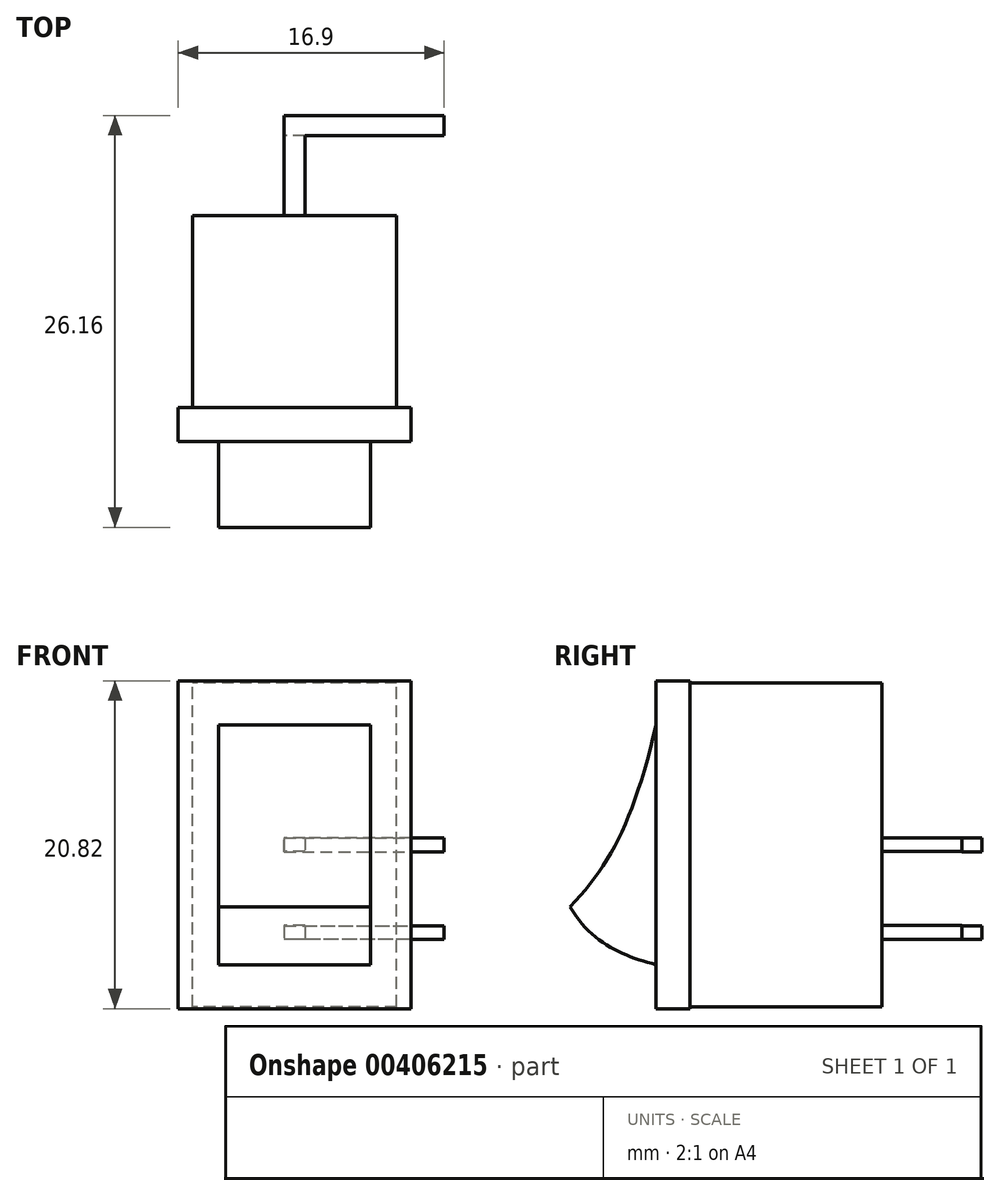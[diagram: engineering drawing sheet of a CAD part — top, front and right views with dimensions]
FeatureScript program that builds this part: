
annotation { "Feature Type Name" : "Feature", "Feature Type Description" : "" }
export const myFeature = defineFeature(function(context is Context, id is Id, definition is map)
    precondition{}
    {
        {
            var Q0;
            Q0=qCreatedBy(makeId("Front.planeOp"),FACE);
            var sketch = newSketch(context, id + "F0", { "sketchPlane" : qUnion([Q0])});
            skLineSegment(sketch, "E0.bottom", {"start": v(4.83, -7.62) * mm, "end": v(-4.83, -7.62) * mm});
            skLineSegment(sketch, "E0.top", {"start": v(4.83, 7.62) * mm, "end": v(-4.83, 7.62) * mm});
            skLineSegment(sketch, "E0.left", {"start": v(4.83, -7.62) * mm, "end": v(4.83, 7.62) * mm});
            skLineSegment(sketch, "E0.right", {"start": v(-4.83, -7.62) * mm, "end": v(-4.83, 7.62) * mm});
            skPoint(sketch, "E0.middle", {"position": v(0, 0) * mm});
            skLineSegment(sketch, "E1.bottom", {"start": v(6.48, -10.29) * mm, "end": v(-6.48, -10.29) * mm});
            skLineSegment(sketch, "E1.top", {"start": v(6.48, 10.29) * mm, "end": v(-6.48, 10.29) * mm});
            skLineSegment(sketch, "E1.left", {"start": v(6.48, -10.29) * mm, "end": v(6.48, 10.29) * mm});
            skLineSegment(sketch, "E1.right", {"start": v(-6.48, -10.29) * mm, "end": v(-6.48, 10.29) * mm});
            skLineSegment(sketch, "E2.bottom", {"start": v(7.4, -10.41) * mm, "end": v(-7.4, -10.41) * mm});
            skLineSegment(sketch, "E2.top", {"start": v(7.4, 10.41) * mm, "end": v(-7.4, 10.41) * mm});
            skLineSegment(sketch, "E2.left", {"start": v(7.4, -10.41) * mm, "end": v(7.4, 10.41) * mm});
            skLineSegment(sketch, "E2.right", {"start": v(-7.4, -10.41) * mm, "end": v(-7.4, 10.41) * mm});
            skSolve(sketch);
        }
        {
            var Q0;
            {var subQ9=sQuery(id+"F0.wireOp",EDGE,"E1.bottom");Q0=makeQuery(id+"F0.imprint","IMPRINT",FACE,{"disambiguationData":[TD([[makeQuery(id+"F0.imprint","IMPRINT",EDGE,{"derivedFrom":subQ9}),1.0]])]});}
            var Q1;
            {var subQ0=sQuery(id+"F0.wireOp",EDGE,"90RDVzbx-pbEp-RKpr-ZJp7-oBMPYdw4tj7I");var subQ1=sQuery(id+"F0.wireOp",EDGE,"E1.left");var subQ2=makeQuery(id+"F0.imprint","INTERSECT",VERTEX,{"derivedFrom":[subQ1,subQ0]});Q1=makeQuery(id+"F0.imprint","IMPRINT",FACE,{"disambiguationData":[TD([[makeQuery(id+"F0.imprint","IMPRINT",EDGE,{"disambiguationData":[TD([[subQ2,-1.0]])],"derivedFrom":subQ1}),-1.0]])]});}
            var Q2;
            {var subQ0=sQuery(id+"F0.wireOp",EDGE,"RYyEcB3p-NkHa-Vshw-HssV-5ZcSdsTJxcc6");var subQ1=sQuery(id+"F0.wireOp",EDGE,"E1.left");var subQ2=makeQuery(id+"F0.imprint","INTERSECT",VERTEX,{"derivedFrom":[subQ1,subQ0]});Q2=makeQuery(id+"F0.imprint","IMPRINT",FACE,{"disambiguationData":[TD([[makeQuery(id+"F0.imprint","IMPRINT",EDGE,{"disambiguationData":[TD([[subQ2,-1.0]])],"derivedFrom":subQ1}),-1.0]])]});}
            var Q3;
            {var subQ0=sQuery(id+"F0.wireOp",EDGE,"IALBhpj6-41kV-CNMg-Mphc-D1CcIKWyzzbN");var subQ1=sQuery(id+"F0.wireOp",EDGE,"E1.left");var subQ2=makeQuery(id+"F0.imprint","INTERSECT",VERTEX,{"derivedFrom":[subQ1,subQ0]});Q3=makeQuery(id+"F0.imprint","IMPRINT",FACE,{"disambiguationData":[TD([[makeQuery(id+"F0.imprint","IMPRINT",EDGE,{"disambiguationData":[TD([[subQ2,-1.0]])],"derivedFrom":subQ1}),-1.0]])]});}
            var Q4;
            {var subQ0=sQuery(id+"F0.wireOp",EDGE,"IALBhpj6-41kV-CNMg-Mphc-D1CcIKWyzzbN");var subQ1=sQuery(id+"F0.wireOp",EDGE,"E0.left");var subQ2=makeQuery(id+"F0.imprint","INTERSECT",VERTEX,{"derivedFrom":[subQ1,subQ0]});Q4=makeQuery(id+"F0.imprint","IMPRINT",FACE,{"disambiguationData":[TD([[makeQuery(id+"F0.imprint","IMPRINT",EDGE,{"disambiguationData":[TD([[subQ2,-1.0]])],"derivedFrom":subQ1}),-1.0]])]});}
            var Q5;
            {var subQ0=sQuery(id+"F0.wireOp",EDGE,"90RDVzbx-pbEp-RKpr-ZJp7-oBMPYdw4tj7I");var subQ1=sQuery(id+"F0.wireOp",EDGE,"E0.left");var subQ2=makeQuery(id+"F0.imprint","INTERSECT",VERTEX,{"derivedFrom":[subQ1,subQ0]});Q5=makeQuery(id+"F0.imprint","IMPRINT",FACE,{"disambiguationData":[TD([[makeQuery(id+"F0.imprint","IMPRINT",EDGE,{"disambiguationData":[TD([[subQ2,-1.0]])],"derivedFrom":subQ1}),-1.0]])]});}
            extrude(context, id + "F1", {"entities" : qUnion([Q0, Q1, Q2, Q3, Q4, Q5]), "depth" : 2.16 * mm});
        }
        {
            var Q0;
            {var subQ7=sQuery(id+"F0.wireOp",EDGE,"E0.bottom");Q0=makeQuery(id+"F0.imprint","IMPRINT",FACE,{"disambiguationData":[TD([[makeQuery(id+"F0.imprint","IMPRINT",EDGE,{"derivedFrom":subQ7}),1.0]])]});}
            var Q1;
            {var subQ0=sQuery(id+"F0.wireOp",EDGE,"RYyEcB3p-NkHa-Vshw-HssV-5ZcSdsTJxcc6");var subQ1=sQuery(id+"F0.wireOp",EDGE,"E0.left");var subQ2=makeQuery(id+"F0.imprint","INTERSECT",VERTEX,{"derivedFrom":[subQ1,subQ0]});Q1=makeQuery(id+"F0.imprint","IMPRINT",FACE,{"disambiguationData":[TD([[makeQuery(id+"F0.imprint","IMPRINT",EDGE,{"disambiguationData":[TD([[subQ2,-1.0]])],"derivedFrom":subQ1}),-1.0]])]});}
            extrude(context, id + "F2", {"entities" : qUnion([Q0, Q1]), "operationType" : NewBodyOperationType.ADD, "depth" : 2.16 * mm});
        }
        {
            var Q0;
            {var subQ7=sQuery(id+"F0.wireOp",EDGE,"E0.bottom");Q0=makeQuery(id+"F0.imprint","IMPRINT",FACE,{"disambiguationData":[TD([[makeQuery(id+"F0.imprint","IMPRINT",EDGE,{"derivedFrom":subQ7}),-1.0]])]});}
            var Q1;
            {var subQ5=sQuery(id+"F0.wireOp",EDGE,"Gz4o4iUm-N9Nq-rkyt-yYwc-V763e9riTsWX");Q1=makeQuery(id+"F0.imprint","IMPRINT",FACE,{"disambiguationData":[TD([[makeQuery(id+"F0.imprint","IMPRINT",EDGE,{"derivedFrom":subQ5}),-1.0]])]});}
            var Q2;
            {var subQ5=sQuery(id+"F0.wireOp",EDGE,"LmZJG6sO-EFJF-EY5x-AEzQ-LZyFRe2Vw74O");Q2=makeQuery(id+"F0.imprint","IMPRINT",FACE,{"disambiguationData":[TD([[makeQuery(id+"F0.imprint","IMPRINT",EDGE,{"derivedFrom":subQ5}),1.0]])]});}
            extrude(context, id + "F3", {"entities" : qUnion([Q0, Q1, Q2]), "operationType" : NewBodyOperationType.ADD, "depth" : 7.62 * mm});
        }
        {
            var Q0;
            {var subQ7=sQuery(id+"F0.wireOp",EDGE,"E0.bottom");Q0=makeQuery(id+"F0.imprint","IMPRINT",FACE,{"disambiguationData":[TD([[makeQuery(id+"F0.imprint","IMPRINT",EDGE,{"derivedFrom":subQ7}),1.0]])]});}
            var Q1;
            {var subQ0=sQuery(id+"F0.wireOp",EDGE,"90RDVzbx-pbEp-RKpr-ZJp7-oBMPYdw4tj7I");var subQ1=sQuery(id+"F0.wireOp",EDGE,"E0.left");var subQ2=makeQuery(id+"F0.imprint","INTERSECT",VERTEX,{"derivedFrom":[subQ1,subQ0]});Q1=makeQuery(id+"F0.imprint","IMPRINT",FACE,{"disambiguationData":[TD([[makeQuery(id+"F0.imprint","IMPRINT",EDGE,{"disambiguationData":[TD([[subQ2,-1.0]])],"derivedFrom":subQ1}),-1.0]])]});}
            var Q2;
            {var subQ0=sQuery(id+"F0.wireOp",EDGE,"RYyEcB3p-NkHa-Vshw-HssV-5ZcSdsTJxcc6");var subQ1=sQuery(id+"F0.wireOp",EDGE,"E0.left");var subQ2=makeQuery(id+"F0.imprint","INTERSECT",VERTEX,{"derivedFrom":[subQ1,subQ0]});Q2=makeQuery(id+"F0.imprint","IMPRINT",FACE,{"disambiguationData":[TD([[makeQuery(id+"F0.imprint","IMPRINT",EDGE,{"disambiguationData":[TD([[subQ2,-1.0]])],"derivedFrom":subQ1}),-1.0]])]});}
            var Q3;
            {var subQ0=sQuery(id+"F0.wireOp",EDGE,"IALBhpj6-41kV-CNMg-Mphc-D1CcIKWyzzbN");var subQ1=sQuery(id+"F0.wireOp",EDGE,"E0.left");var subQ2=makeQuery(id+"F0.imprint","INTERSECT",VERTEX,{"derivedFrom":[subQ1,subQ0]});Q3=makeQuery(id+"F0.imprint","IMPRINT",FACE,{"disambiguationData":[TD([[makeQuery(id+"F0.imprint","IMPRINT",EDGE,{"disambiguationData":[TD([[subQ2,-1.0]])],"derivedFrom":subQ1}),-1.0]])]});}
            var Q4;
            {var subQ7=sQuery(id+"F0.wireOp",EDGE,"E0.bottom");Q4=makeQuery(id+"F0.imprint","IMPRINT",FACE,{"disambiguationData":[TD([[makeQuery(id+"F0.imprint","IMPRINT",EDGE,{"derivedFrom":subQ7}),-1.0]])]});}
            var Q5;
            {var subQ5=sQuery(id+"F0.wireOp",EDGE,"Gz4o4iUm-N9Nq-rkyt-yYwc-V763e9riTsWX");Q5=makeQuery(id+"F0.imprint","IMPRINT",FACE,{"disambiguationData":[TD([[makeQuery(id+"F0.imprint","IMPRINT",EDGE,{"derivedFrom":subQ5}),-1.0]])]});}
            var Q6;
            {var subQ5=sQuery(id+"F0.wireOp",EDGE,"LmZJG6sO-EFJF-EY5x-AEzQ-LZyFRe2Vw74O");Q6=makeQuery(id+"F0.imprint","IMPRINT",FACE,{"disambiguationData":[TD([[makeQuery(id+"F0.imprint","IMPRINT",EDGE,{"derivedFrom":subQ5}),1.0]])]});}
            extrude(context, id + "F4", {"entities" : qUnion([Q0, Q1, Q2, Q3, Q4, Q5, Q6]), "operationType" : NewBodyOperationType.ADD, "oppositeDirection" : true, "depth" : 12.2 * mm});
        }
        {
            var Q0;
            Q0=makeQuery(id+"F3.opExtrude","SWEPT_FACE",FACE,{"disambiguationData":[OSD([sQuery(id+"F0.wireOp",EDGE,"E0.right")])]});
            var sketch = newSketch(context, id + "F5", { "sketchPlane" : qUnion([Q0])});
            skFitSpline(sketch, "E3", {"points": [v(2.16, -7.62) * mm, v(7.62, -3.94) * mm], "startDerivative": vector(6.36, 1.68) * mm, "endDerivative": vector(3.97, 6.9) * mm});
            skFitSpline(sketch, "E4", {"points": [v(7.62, -3.94) * mm, v(2.16, 7.62) * mm], "startDerivative": vector(-7.88, 8.25) * mm, "endDerivative": vector(-4.33, 18.23) * mm});
            skSolve(sketch);
        }
        {
            var Q0;
            {var subQ0=sQuery(id+"F5.wireOp",EDGE,"E3");Q0=makeQuery(id+"F5.imprint","IMPRINT",FACE,{"disambiguationData":[TD([[makeQuery(id+"F5.imprint","IMPRINT",EDGE,{"derivedFrom":subQ0}),-1.0]])]});}
            extrude(context, id + "F6", {"entities" : qUnion([Q0]), "operationType" : NewBodyOperationType.REMOVE, "oppositeDirection" : true, "depth" : 25.4 * mm});
        }
        {
            var Q0;
            {var subQ0=sQuery(id+"F5.wireOp",EDGE,"E4");Q0=makeQuery(id+"F5.imprint","IMPRINT",FACE,{"disambiguationData":[TD([[makeQuery(id+"F5.imprint","IMPRINT",EDGE,{"derivedFrom":subQ0}),-1.0]])]});}
            extrude(context, id + "F7", {"entities" : qUnion([Q0]), "operationType" : NewBodyOperationType.REMOVE, "oppositeDirection" : true, "depth" : 25.4 * mm});
        }
        {
            var Q0;
            Q0=makeQuery(id+"F4.opExtrude","CAP_FACE",FACE,{"disambiguationData":[OSD([sQuery(id+"F0.wireOp",EDGE,"E1.bottom"),sQuery(id+"F0.wireOp",EDGE,"E1.top"),sQuery(id+"F0.wireOp",EDGE,"E1.left"),sQuery(id+"F0.wireOp",EDGE,"E1.right")])],"isStart":false});
            var sketch = newSketch(context, id + "F8", { "sketchPlane" : qUnion([Q0])});
            skLineSegment(sketch, "E5", {"start": v(0, 0) * mm, "end": v(0, 0) * mm});
            skLineSegment(sketch, "E6.bottom", {"start": v(-0.66, 0.43) * mm, "end": v(0.66, 0.43) * mm});
            skLineSegment(sketch, "E6.top", {"start": v(-0.66, -0.43) * mm, "end": v(0.66, -0.43) * mm});
            skLineSegment(sketch, "E6.left", {"start": v(-0.66, 0.43) * mm, "end": v(-0.66, -0.43) * mm});
            skLineSegment(sketch, "E6.right", {"start": v(0.66, 0.43) * mm, "end": v(0.66, -0.43) * mm});
            skPoint(sketch, "E6.middle", {"position": v(0, 0) * mm});
            skLineSegment(sketch, "E7.bottom", {"start": v(-0.66, -5.13) * mm, "end": v(0.66, -5.13) * mm});
            skLineSegment(sketch, "E7.top", {"start": v(-0.66, -6) * mm, "end": v(0.66, -6) * mm});
            skLineSegment(sketch, "E7.left", {"start": v(-0.66, -5.13) * mm, "end": v(-0.66, -6) * mm});
            skLineSegment(sketch, "E7.right", {"start": v(0.66, -5.13) * mm, "end": v(0.66, -6) * mm});
            skPoint(sketch, "E7.middle", {"position": v(0, -5.57) * mm});
            skSolve(sketch);
        }
        {
            var Q0;
            Q0=makeQuery(id+"F8.imprint","IMPRINT",FACE,{"disambiguationData":[TD([[makeQuery(id+"F8.imprint","IMPRINT",EDGE,{"derivedFrom":sQuery(id+"F8.wireOp",EDGE,"E6.bottom")}),-1.0]])]});
            var Q1;
            Q1=makeQuery(id+"F8.imprint","IMPRINT",FACE,{"disambiguationData":[TD([[makeQuery(id+"F8.imprint","IMPRINT",EDGE,{"derivedFrom":sQuery(id+"F8.wireOp",EDGE,"E7.bottom")}),-1.0]])]});
            extrude(context, id + "F9", {"entities" : qUnion([Q0, Q1]), "operationType" : NewBodyOperationType.ADD, "depth" : 5.08 * mm});
        }
        {
            var Q0;
            Q0=makeQuery(id+"F9.opExtrude","CAP_FACE",FACE,{"disambiguationData":[OSD([sQuery(id+"F8.wireOp",EDGE,"E7.bottom"),sQuery(id+"F8.wireOp",EDGE,"E7.top"),sQuery(id+"F8.wireOp",EDGE,"E7.left"),sQuery(id+"F8.wireOp",EDGE,"E7.right")])],"isStart":false});
            var sketch = newSketch(context, id + "F10", { "sketchPlane" : qUnion([Q0])});
            skLineSegment(sketch, "E8.bottom", {"start": v(0.66, -6) * mm, "end": v(-9.5, -6) * mm});
            skLineSegment(sketch, "E8.top", {"start": v(0.66, -5.15) * mm, "end": v(-9.5, -5.15) * mm});
            skLineSegment(sketch, "E8.left", {"start": v(0.66, -6) * mm, "end": v(0.66, -5.15) * mm});
            skLineSegment(sketch, "E8.right", {"start": v(-9.5, -6) * mm, "end": v(-9.5, -5.15) * mm});
            skLineSegment(sketch, "E9.bottom", {"start": v(0.66, -0.44) * mm, "end": v(-9.5, -0.44) * mm});
            skLineSegment(sketch, "E9.top", {"start": v(0.66, 0.42) * mm, "end": v(-9.5, 0.42) * mm});
            skLineSegment(sketch, "E9.left", {"start": v(0.66, -0.44) * mm, "end": v(0.66, 0.42) * mm});
            skLineSegment(sketch, "E9.right", {"start": v(-9.5, -0.44) * mm, "end": v(-9.5, 0.42) * mm});
            skSolve(sketch);
        }
        {
            var Q0;
            Q0=makeQuery(id+"F10.imprint","IMPRINT",FACE,{"disambiguationData":[TD([[makeQuery(id+"F10.imprint","IMPRINT",EDGE,{"derivedFrom":sQuery(id+"F10.wireOp",EDGE,"E9.bottom")}),-1.0]])]});
            var Q1;
            {var subQ3=sQuery(id+"F10.wireOp",EDGE,"E8.left");Q1=makeQuery(id+"F10.imprint","IMPRINT",FACE,{"disambiguationData":[TD([[makeQuery(id+"F10.imprint","IMPRINT",EDGE,{"derivedFrom":subQ3}),-1.0]])]});}
            var Q2;
            {var subQ3=sQuery(id+"F10.wireOp",EDGE,"E8.right");Q2=makeQuery(id+"F10.imprint","IMPRINT",FACE,{"disambiguationData":[TD([[makeQuery(id+"F10.imprint","IMPRINT",EDGE,{"derivedFrom":subQ3}),-1.0]])]});}
            extrude(context, id + "F11", {"entities" : qUnion([Q0, Q1, Q2]), "operationType" : NewBodyOperationType.ADD, "depth" : 1.27 * mm});
        }
    });
